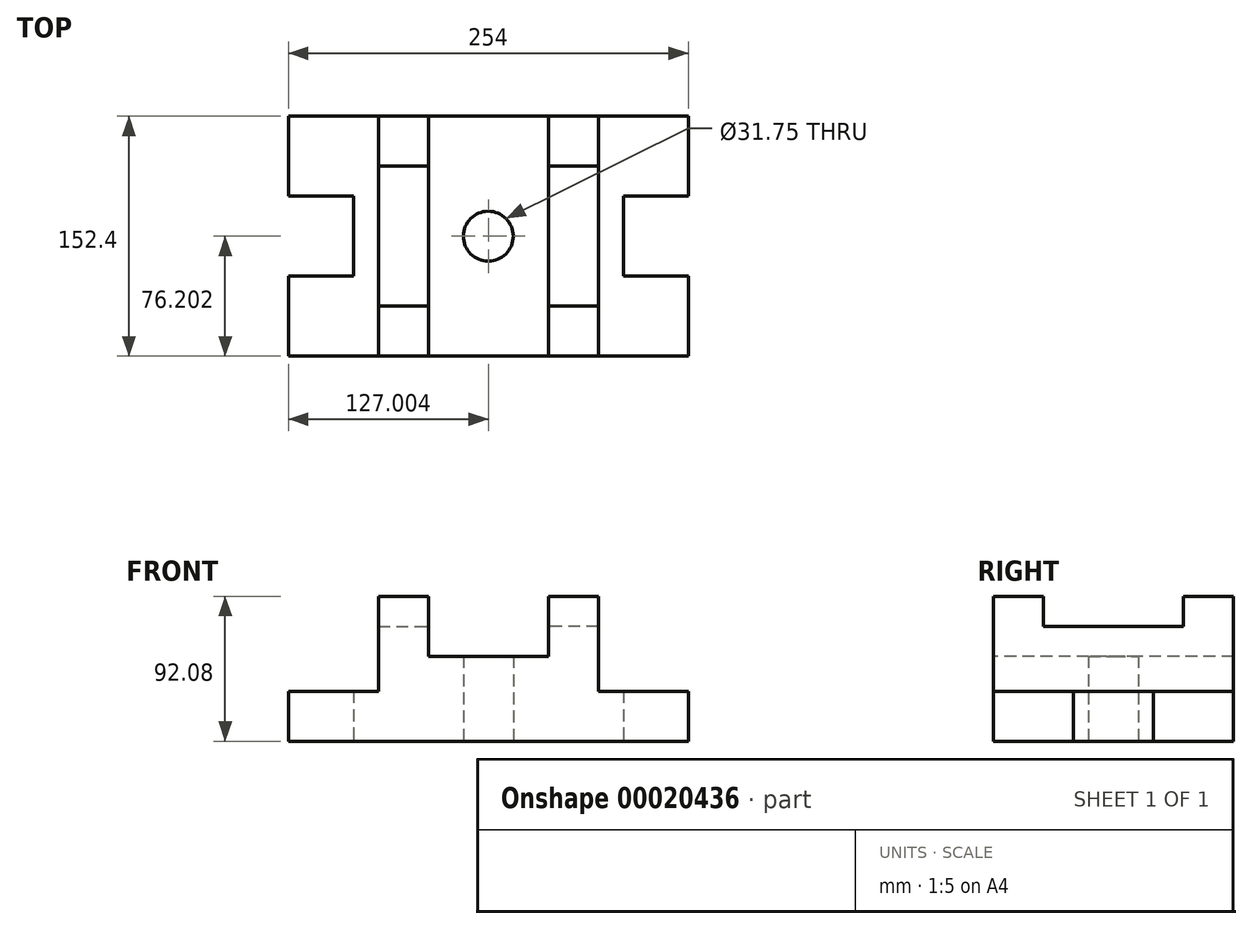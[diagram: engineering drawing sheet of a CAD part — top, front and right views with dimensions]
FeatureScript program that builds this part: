
annotation { "Feature Type Name" : "Feature", "Feature Type Description" : "" }
export const myFeature = defineFeature(function(context is Context, id is Id, definition is map)
    precondition{}
    {
        {
            var Q0;
            Q0=qCreatedBy(makeId("Top.planeOp"),FACE);
            var sketch = newSketch(context, id + "F0", { "sketchPlane" : qUnion([Q0])});
            skLineSegment(sketch, "E0", {"start": v(76.67, -7.98) * mm, "end": v(76.67, -58.78) * mm});
            skLineSegment(sketch, "E1", {"start": v(76.67, -7.98) * mm, "end": v(35.4, -7.98) * mm});
            skLineSegment(sketch, "E2", {"start": v(35.4, -7.98) * mm, "end": v(35.4, 42.82) * mm});
            skLineSegment(sketch, "E3", {"start": v(35.4, 42.82) * mm, "end": v(76.67, 42.82) * mm});
            skLineSegment(sketch, "E4", {"start": v(76.67, 42.82) * mm, "end": v(76.67, 93.62) * mm});
            skLineSegment(sketch, "E5", {"start": v(76.67, 93.62) * mm, "end": v(19.52, 93.62) * mm});
            skLineSegment(sketch, "E6", {"start": v(19.52, -58.78) * mm, "end": v(76.67, -58.78) * mm});
            skLineSegment(sketch, "E7", {"start": v(19.52, 93.62) * mm, "end": v(-12.23, 93.62) * mm});
            skLineSegment(sketch, "E8", {"start": v(19.52, -58.78) * mm, "end": v(-50.33, -58.78) * mm});
            skLineSegment(sketch, "E9", {"start": v(-12.23, 93.62) * mm, "end": v(-50.33, 93.62) * mm});
            skLineSegment(sketch, "E10", {"start": v(-50.33, 93.62) * mm, "end": v(-50.33, -58.78) * mm});
            skLineSegment(sketch, "E11", {"start": v(-12.23, 93.62) * mm, "end": v(-12.23, 61.87) * mm});
            skLineSegment(sketch, "E12", {"start": v(19.52, 93.62) * mm, "end": v(19.52, 61.87) * mm});
            skLineSegment(sketch, "E13", {"start": v(-12.23, 61.87) * mm, "end": v(19.52, 61.87) * mm});
            skLineSegment(sketch, "E14", {"start": v(19.52, -58.78) * mm, "end": v(19.52, -27.03) * mm});
            skLineSegment(sketch, "E15", {"start": v(19.52, -27.03) * mm, "end": v(-12.23, -27.03) * mm});
            skLineSegment(sketch, "E16", {"start": v(-12.23, -27.03) * mm, "end": v(-12.23, -58.78) * mm});
            skLineSegment(sketch, "E17", {"start": v(-12.23, 61.87) * mm, "end": v(-12.23, -27.03) * mm});
            skLineSegment(sketch, "E18", {"start": v(19.52, 61.87) * mm, "end": v(19.52, -27.03) * mm});
            skCircle(sketch, "E19", {"center": v(-50.33, 17.42) * mm, "radius": 15.88 * mm});
            skSolve(sketch);
        }
        {
            var Q0;
            Q0=makeQuery(id+"F0.imprint","IMPRINT",FACE,{"disambiguationData":[TD([[makeQuery(id+"F0.imprint","IMPRINT",EDGE,{"derivedFrom":sQuery(id+"F0.wireOp",EDGE,"E0")}),-1.0]])]});
            extrude(context, id + "F1", {"entities" : qUnion([Q0]), "depth" : 31.75 * mm});
        }
        {
            var Q0;
            Q0=makeQuery(id+"F0.imprint","IMPRINT",FACE,{"disambiguationData":[TD([[makeQuery(id+"F0.imprint","IMPRINT",EDGE,{"derivedFrom":sQuery(id+"F0.wireOp",EDGE,"E9")}),1.0]])]});
            extrude(context, id + "F2", {"entities" : qUnion([Q0]), "depth" : 53.97 * mm});
        }
        {
            var Q0;
            {var subQ1=sQuery(id+"F0.wireOp",EDGE,"E14");Q0=makeQuery(id+"F0.imprint","IMPRINT",FACE,{"disambiguationData":[TD([[makeQuery(id+"F0.imprint","IMPRINT",EDGE,{"derivedFrom":subQ1}),1.0]])]});}
            var Q1;
            Q1=makeQuery(id+"F0.imprint","IMPRINT",FACE,{"disambiguationData":[TD([[makeQuery(id+"F0.imprint","IMPRINT",EDGE,{"derivedFrom":sQuery(id+"F0.wireOp",EDGE,"E7")}),1.0]])]});
            var Q2;
            Q2=makeQuery(id+"F0.imprint","IMPRINT",FACE,{"disambiguationData":[TD([[makeQuery(id+"F0.imprint","IMPRINT",EDGE,{"derivedFrom":sQuery(id+"F0.wireOp",EDGE,"E13")}),-1.0]])]});
            extrude(context, id + "F3", {"entities" : qUnion([Q0, Q1, Q2]), "depth" : 73.02 * mm});
        }
        {
            var Q0;
            {var subQ1=sQuery(id+"F0.wireOp",EDGE,"E14");Q0=makeQuery(id+"F0.imprint","IMPRINT",FACE,{"disambiguationData":[TD([[makeQuery(id+"F0.imprint","IMPRINT",EDGE,{"derivedFrom":subQ1}),1.0]])]});}
            var Q1;
            Q1=makeQuery(id+"F0.imprint","IMPRINT",FACE,{"disambiguationData":[TD([[makeQuery(id+"F0.imprint","IMPRINT",EDGE,{"derivedFrom":sQuery(id+"F0.wireOp",EDGE,"E7")}),1.0]])]});
            extrude(context, id + "F4", {"entities" : qUnion([Q0, Q1]), "depth" : 92.07 * mm});
        }
        {
            var Q0;
            Q0=makeQuery(id+"F3.opExtrude","SWEPT_BODY",BODY,{"disambiguationData":[OSD([sQuery(id+"F0.wireOp",EDGE,"E7"),sQuery(id+"F0.wireOp",EDGE,"E8"),sQuery(id+"F0.wireOp",EDGE,"E11"),sQuery(id+"F0.wireOp",EDGE,"E12"),sQuery(id+"F0.wireOp",EDGE,"E14"),sQuery(id+"F0.wireOp",EDGE,"E16"),sQuery(id+"F0.wireOp",EDGE,"E17"),sQuery(id+"F0.wireOp",EDGE,"E18")])]});
            var Q1;
            Q1=makeQuery(id+"F2.opExtrude","SWEPT_BODY",BODY,{"disambiguationData":[OSD([sQuery(id+"F0.wireOp",EDGE,"E8"),sQuery(id+"F0.wireOp",EDGE,"E9"),sQuery(id+"F0.wireOp",EDGE,"E10"),sQuery(id+"F0.wireOp",EDGE,"E11"),sQuery(id+"F0.wireOp",EDGE,"E16"),sQuery(id+"F0.wireOp",EDGE,"E17"),sQuery(id+"F0.wireOp",EDGE,"E19")])]});
            var Q2;
            Q2=makeQuery(id+"F4.opExtrude","SWEPT_BODY",BODY,{"disambiguationData":[OSD([sQuery(id+"F0.wireOp",EDGE,"E7"),sQuery(id+"F0.wireOp",EDGE,"E11"),sQuery(id+"F0.wireOp",EDGE,"E12"),sQuery(id+"F0.wireOp",EDGE,"E13")])]});
            var Q3;
            Q3=makeQuery(id+"F4.opExtrude","SWEPT_BODY",BODY,{"disambiguationData":[OSD([sQuery(id+"F0.wireOp",EDGE,"E8"),sQuery(id+"F0.wireOp",EDGE,"E14"),sQuery(id+"F0.wireOp",EDGE,"E15"),sQuery(id+"F0.wireOp",EDGE,"E16")])]});
            var Q4;
            Q4=makeQuery(id+"F1.opExtrude","SWEPT_BODY",BODY,{"disambiguationData":[OSD([sQuery(id+"F0.wireOp",EDGE,"E0"),sQuery(id+"F0.wireOp",EDGE,"E1"),sQuery(id+"F0.wireOp",EDGE,"E2"),sQuery(id+"F0.wireOp",EDGE,"E3"),sQuery(id+"F0.wireOp",EDGE,"E4"),sQuery(id+"F0.wireOp",EDGE,"E5"),sQuery(id+"F0.wireOp",EDGE,"E6"),sQuery(id+"F0.wireOp",EDGE,"E12"),sQuery(id+"F0.wireOp",EDGE,"E14"),sQuery(id+"F0.wireOp",EDGE,"E18")])]});
            var Q5;
            {var subQ0=sQuery(id+"F0.wireOp",EDGE,"E10");Q5=makeQuery(id+"F2.opExtrude","SWEPT_FACE",FACE,{"disambiguationData":[OSD([subQ0]),TDD([makeQuery(id+"F0.imprint","IMPRINT",EDGE,{"disambiguationData":[TD([[makeQuery(id+"F0.imprint","INTERSECT",VERTEX,{"derivedFrom":[sQuery(id+"F0.wireOp",EDGE,"E9"),subQ0]}),-1.0]])],"derivedFrom":subQ0})])]});}
            mirror(context, id + "F5", {"operationType" : NewBodyOperationType.ADD, "entities" : qUnion([Q0, Q1, Q2, Q3, Q4]), "mirrorPlane" : qUnion([Q5])});
        }
    });
